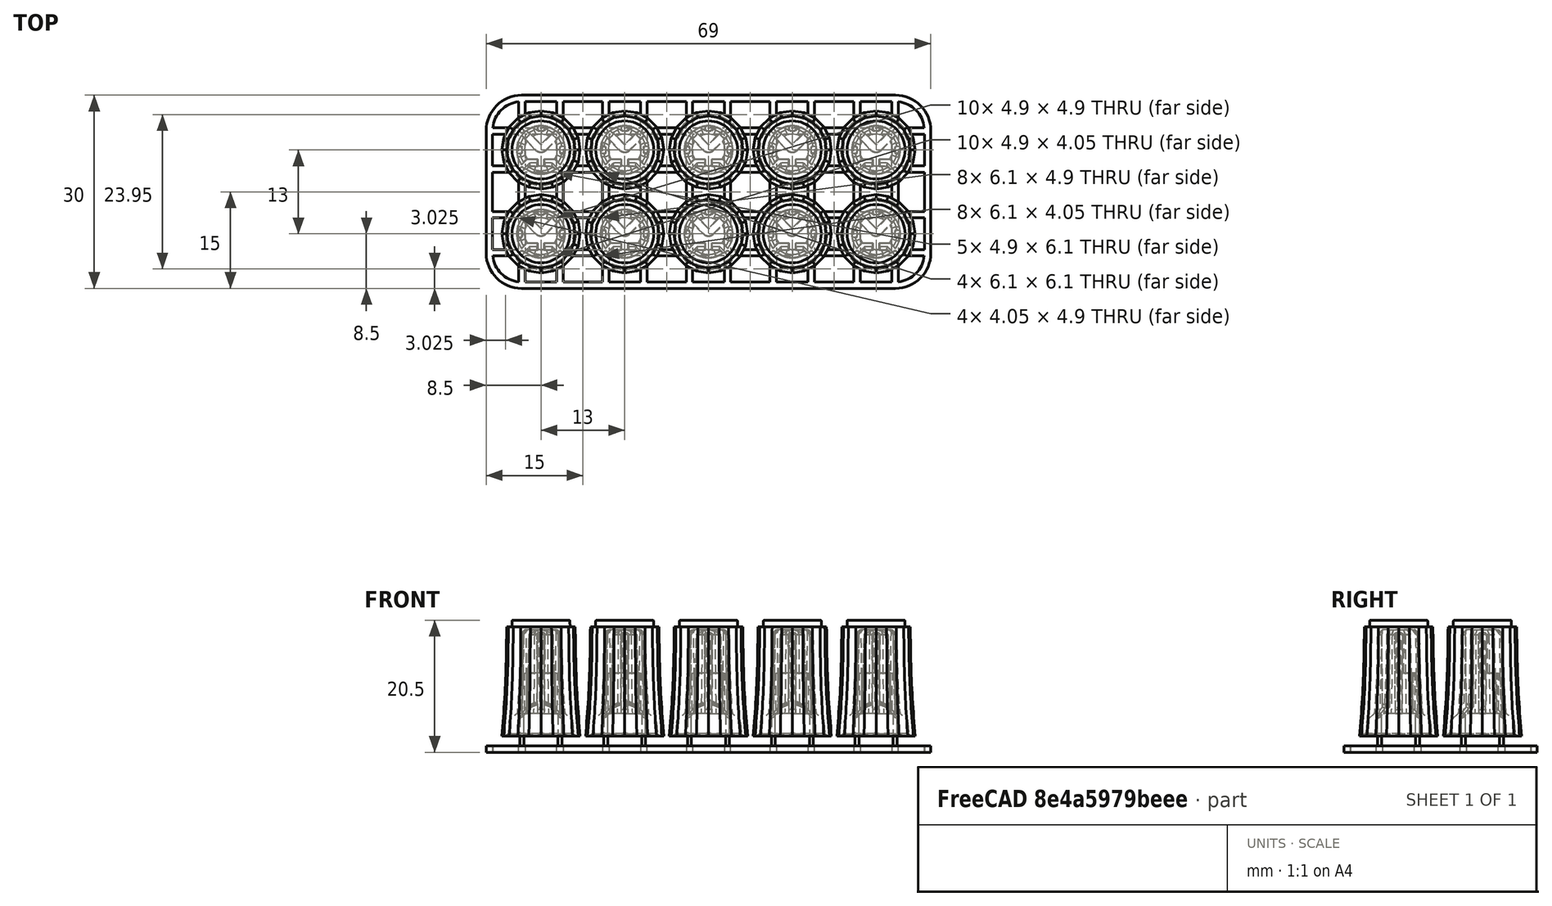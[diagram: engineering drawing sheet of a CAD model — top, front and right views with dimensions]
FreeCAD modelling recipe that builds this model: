
FCSTD DOCUMENT  (FreeCAD 1.0R38641 +678 (Git))
Label: PLASTIC-KNOB-ENC_printable
License: All rights reserved
LicenseURL: https://en.wikipedia.org/wiki/All_rights_reserved
objects: TechDraw::DrawViewDimension×11, TechDraw::DrawHatch×10, Sketcher::SketchObject×8, TechDraw::DrawViewBalloon×5, PartDesign::Pad×5, TechDraw::DrawViewPart×5, PartDesign::PolarPattern×3, TechDraw::DrawViewAnnotation×2, PartDesign::Pocket×2, PartDesign::Plane×2, PartDesign::LinearPattern×2, Part::Feature×1, PartDesign::Boolean×1, TechDraw::DrawSVGTemplate×1, PartDesign::Mirrored×1, PartDesign::CoordinateSystem×1, PartDesign::MultiTransform×1, PartDesign::Body×1, TechDraw::DrawComplexSection×1, TechDraw::DrawPage×1
note: 79 computed .brp shape members not serialized (recipe doc carries the construction recipe); baked Part::Feature solids carry a one-line shape summary decoded from their .brp

FEATURE [Part::Feature] Part__Feature  label="potmeter"
  shape: bbox 15.71 x 15.32 x 34.99 mm, 134 faces (baked)
FEATURE [PartDesign::Boolean] Boolean
  Group = -> [Part__Feature]
  Suppressed = false
  Type = 0
  UsePlacement = false
FEATURE [TechDraw::DrawSVGTemplate] Template
  EditableTexts = COLOR=Black - RAL code: 9004; CreationDate=2025-07-31; E.G.APPROVED=APPROVED; FC-Scale=5:1; FC-Title=PLASTIC - KNOB - POT; IntechStudioLtd.=Intech Studio Ltd.; MATERIAL=ABS - Terluran GP22; REV=03; STANDARD=DIN 16742-TG4
  Height = 297
  Orientation = 1
  Template = <userpath>/Documents/grid-hardware/Manufacturing/FreeCAD_technical_drawing_template/A3_LandscapeTD_MODIFIED.svg
  Width = 420
FEATURE [Sketcher::SketchObject] Sketch
  ArcFitTolerance = 0
  AttachmentSupport = -> [XZ_Plane]
  FullyConstrained = true
  MakeInternals = false
  MapMode = 5
  Placement = pos=(0,0,0) rot=(1,0,0;1.5708rad)
  sketch-geometry (1):
    g0: LineSegment StartX=0 StartY=19 StartZ=0 EndX=0 EndY=-1 EndZ=0
  constraints (4):
    c: PointOnObject(g0,g-2)
    c: Vertical(g0)
    c: DistanceY(g0,g0) = 20
    c: DistanceY(g0,g-1) = 1
FEATURE [TechDraw::DrawViewDimension] Dimension010
  AngleOverride = false
  Arbitrary = false
  ArbitraryTolerances = false
  EqualTolerance = true
  ExtensionAngle = 0
  FormatSpec = %.2w
  FormatSpecOverTolerance = %+.2w
  FormatSpecUnderTolerance = %+.2w
  Inverted = false
  LineAngle = 0
  LockPosition = false
  MeasureType = 1
  OverTolerance = 0
  Rotation = 0
  ScaleType = 0
  TheoreticalExact = false
  Type = 2
  UnderTolerance = 0
  X = -41.9183
  Y = 15.656
FEATURE [TechDraw::DrawViewAnnotation] Annotation001
  Font = osifont
  LineSpace = 100
  LockPosition = false
  MaxWidth = -1
  Rotation = 0
  ScaleType = 0
  Text = AESTHETICAL SURFACES: | COLORED BLUE ON THE ISOMETRIC VIEWS: SPI - D2 | NO BURRS, NO PARTING LINES, | NO EJECTION MARKS | FREE OF ANY DEFECTS | FREE OF ANY WELD OR MELD LINES | NON VISIBLE GATE LOCATION ALLOWED | REMAINING BLACK SURFACES: SPI - B2
  TextSize = 3
  TextStyle = 0
  X = 264.167
  Y = 100.12
FEATURE [TechDraw::DrawViewDimension] Dimension012
  AngleOverride = false
  Arbitrary = false
  ArbitraryTolerances = false
  EqualTolerance = true
  ExtensionAngle = 0
  FormatSpec = (%.2w)
  FormatSpecOverTolerance = %+.2w
  FormatSpecUnderTolerance = %+.2w
  Inverted = false
  LineAngle = 0
  LockPosition = false
  MeasureType = 1
  OverTolerance = 0
  Rotation = 0
  ScaleType = 0
  TheoreticalExact = false
  Type = 2
  UnderTolerance = 0
  X = -37.4834
  Y = -5.49655
FEATURE [TechDraw::DrawViewBalloon] Balloon004
  BubbleShape = 2
  EndType = 6
  EndTypeScale = 1
  KinkLength = 0
  LockPosition = false
  OriginX = -50.6224
  OriginY = 14.8162
  Rotation = 0
  ScaleType = 0
  ShapeScale = 1
  SourceView = -> Dimension010
  Text = 2
  TextWrapLen = -1
  X = -51.7505
  Y = 12.4076
FEATURE [TechDraw::DrawViewAnnotation] Annotation002
  Font = osifont
  LineSpace = 100
  LockPosition = false
  MaxWidth = -1
  Rotation = 0
  ScaleType = 0
  Text = Section A-A
  TextSize = 4
  TextStyle = 0
  X = 193.568
  Y = 128.632
FEATURE [Sketcher::SketchObject] Sketch008
  ArcFitTolerance = 0
  AttachmentSupport = -> [XY_Plane]
  FullyConstrained = true
  MakeInternals = false
  MapMode = 5
  sketch-geometry (6):
    g0: ArcOfCircle CenterX=0 CenterY=0 CenterZ=0 NormalX=0 NormalY=0 NormalZ=1 AngleXU=0 Radius=2.95 StartAngle=0.615084 EndAngle=0.955712
    g1: LineSegment StartX=2.40934 StartY=1.70223 StartZ=0 EndX=2.05578 EndY=1.34868 EndZ=0
    g2: LineSegment StartX=2.05578 StartY=1.34868 StartZ=0 EndX=1.34868 EndY=2.05578 EndZ=0
    g3: LineSegment StartX=1.34868 StartY=2.05578 StartZ=0 EndX=1.70223 EndY=2.40934 EndZ=0
    g4: LineSegment [constr] StartX=2.08597 StartY=2.08597 StartZ=0 EndX=0 EndY=0 EndZ=0
    g5: GeomPoint [constr] X=1.70223 Y=1.70223 Z=0
  constraints (16):
    c: Coincident(g0,g-1)
    c: Diameter(g0) = 5.9
    c: Coincident(g2,g1)
    c: Coincident(g3,g2)
    c: PointOnObject(g4,g0)
    c: Coincident(g4,g0)
    c: Angle(g4,g-2) = 0.785398
    c: Parallel(g1,g4)
    c: Parallel(g4,g3)
    c: Perpendicular(g1,g2)
    c: Symmetric(g1,g2,g5)
    c: PointOnObject(g5,g4)
    c: Distance(g2) = 1
    c: Distance(g3) = 0.5
    c: Coincident(g0,g3)
    c: Coincident(g0,g1)
FEATURE [PartDesign::Pocket] Pocket
  BaseFeature = -> Boolean
  Direction = (0,0,-1)
  Length = 9.8
  Length2 = 5
  Profile = -> Sketch008
  ReferenceAxis = -> Sketch008 [N_Axis]
  Refine = true
  Reversed = true
  Suppressed = false
  Type = 0
FEATURE [PartDesign::Mirrored] Mirrored
  BaseFeature = -> Pocket
  MirrorPlane = -> Sketch008 [V_Axis]
  Originals = -> [Pocket]
  Refine = true
  Suppressed = false
  TransformMode = 0
FEATURE [Sketcher::SketchObject] Sketch009
  ArcFitTolerance = 0
  AttachmentSupport = -> [XY_Plane]
  FullyConstrained = true
  MakeInternals = false
  MapMode = 5
  sketch-geometry (5):
    g0: ArcOfCircle CenterX=0 CenterY=0 CenterZ=0 NormalX=0 NormalY=0 NormalZ=1 AngleXU=0 Radius=2.95 StartAngle=6.11287 EndAngle=6.4535
    g1: LineSegment StartX=2.90732 StartY=0.5 StartZ=0 EndX=2.40732 EndY=0.5 EndZ=0
    g2: LineSegment StartX=2.40732 StartY=0.5 StartZ=0 EndX=2.40732 EndY=-0.5 EndZ=0
    g3: LineSegment StartX=2.40732 StartY=-0.5 StartZ=0 EndX=2.90732 EndY=-0.5 EndZ=0
    g4: GeomPoint [constr] X=2.40732 Y=0 Z=0
  constraints (13):
    c: Coincident(g0,g-1)
    c: Diameter(g0) = 5.9
    c: Horizontal(g1)
    c: Coincident(g2,g1)
    c: Vertical(g2)
    c: Horizontal(g3)
    c: Coincident(g2,g3)
    c: Symmetric(g1,g2,g4)
    c: PointOnObject(g4,g-1)
    c: DistanceX(g1,g1) = 0.5
    c: DistanceY(g2,g2) = 1
    c: Coincident(g0,g1)
    c: Coincident(g0,g3)
FEATURE [PartDesign::Pocket] Pocket001
  BaseFeature = -> Mirrored
  Direction = (0,0,-1)
  Length = 16.5
  Length2 = 5
  Profile = -> Sketch009
  ReferenceAxis = -> Sketch009 [N_Axis]
  Refine = true
  Reversed = true
  Suppressed = false
  Type = 0
FEATURE [PartDesign::Plane] DatumPlane
  AttachmentOffset = pos=(0,0,0) rot=(0,-1,0;0.15708rad)
  AttachmentSupport = -> [XZ_Plane]
  Length = 105.854
  MapMode = 5
  Placement = pos=(0,0,0) rot=(0.993863,-0.078219,-0.078219;1.57695rad)
  ResizeMode = 0
  Width = 63.5845
FEATURE [Sketcher::SketchObject] Sketch010
  ArcFitTolerance = 0
  AttachmentSupport = -> [DatumPlane]
  FullyConstrained = true
  MakeInternals = false
  MapMode = 5
  Placement = pos=(0,0,0) rot=(0.993863,-0.078219,-0.078219;1.57695rad)
  sketch-geometry (3):
    g0: LineSegment StartX=2.50536 StartY=16.5 StartZ=0 EndX=3.50536 EndY=15.4768 EndZ=0
    g1: LineSegment StartX=2.50536 StartY=16.5 StartZ=0 EndX=3.50536 EndY=16.5 EndZ=0
    g2: LineSegment StartX=3.50536 StartY=16.5 StartZ=0 EndX=3.50536 EndY=15.4768 EndZ=0
  constraints (9):
    c: DistanceY(g-1,g0) = 16.5
    c: DistanceX(g-1,g0) = 2.50536
    c: DistanceX(g0,g0) = 1
    c: Coincident(g1,g0)
    c: Coincident(g2,g1)
    c: Coincident(g2,g0)
    c: Horizontal(g1)
    c: Vertical(g2)
    c: Angle(g0,g1) = 0.796848
FEATURE [PartDesign::PolarPattern] PolarPattern
  Angle = 180
  Axis = -> Sketch009 [N_Axis]
  BaseFeature = -> Pocket001
  Mode = 0
  Occurrences = 3
  Offset = 120
  Originals = -> [Pocket001]
  Refine = true
  Suppressed = false
  TransformMode = 0
FEATURE [PartDesign::Pad] Pad001
  BaseFeature = -> PolarPattern
  Direction = (-0.156434,-0.987688,0)
  Length = 2
  Length2 = 10
  Midplane = true
  Profile = -> Sketch010
  ReferenceAxis = -> Sketch010 [N_Axis]
  Suppressed = false
  Type = 0
FEATURE [PartDesign::Plane] DatumPlane001
  AttachmentOffset = pos=(0,0,0) rot=(0,1,0;0.15708rad)
  AttachmentSupport = -> [XZ_Plane]
  Length = 105.854
  MapMode = 5
  Placement = pos=(0,0,0) rot=(0.993863,0.078219,0.078219;1.57695rad)
  ResizeMode = 0
  Width = 63.5845
FEATURE [Sketcher::SketchObject] Sketch011
  ArcFitTolerance = 0
  AttachmentSupport = -> [DatumPlane001]
  FullyConstrained = true
  MakeInternals = false
  MapMode = 5
  Placement = pos=(0,0,0) rot=(0.993863,0.078219,0.078219;1.57695rad)
  sketch-geometry (3):
    g0: LineSegment StartX=2.50536 StartY=16.5 StartZ=0 EndX=3.50536 EndY=15.4768 EndZ=0
    g1: LineSegment StartX=3.50536 StartY=15.4768 StartZ=0 EndX=3.50536 EndY=16.5 EndZ=0
    g2: LineSegment StartX=3.50536 StartY=16.5 StartZ=0 EndX=2.50536 EndY=16.5 EndZ=0
  constraints (9):
    c: Coincident(g1,g0)
    c: Vertical(g1)
    c: Coincident(g2,g1)
    c: Coincident(g2,g0)
    c: Horizontal(g2)
    c: DistanceX(g0,g0) = 1
    c: DistanceY(g-1,g0) = 16.5
    c: DistanceX(g-1,g0) = 2.50536
    c: Angle(g0,g2) = 0.796848
FEATURE [PartDesign::Pad] Pad002
  BaseFeature = -> Pad001
  Direction = (0.156434,-0.987688,0)
  Length = 2
  Length2 = 10
  Midplane = true
  Profile = -> Sketch011
  ReferenceAxis = -> Sketch011 [N_Axis]
  Suppressed = false
  Type = 0
FEATURE [PartDesign::PolarPattern] PolarPattern001
  Angle = 180
  Axis = -> Z_Axis
  BaseFeature = -> Pad002
  Mode = 0
  Occurrences = 3
  Offset = 120
  Originals = -> [Pad001,Pad002]
  Suppressed = false
  TransformMode = 0
FEATURE [PartDesign::CoordinateSystem] LCS_1
  AttacherType = Attacher::AttachEngine3D
  AttachmentSupport = -> [PolarPattern001]
  MapMode = 5
  Placement = pos=(0,0,9.8) rot=(1,0,0;3.14159rad)
FEATURE [Sketcher::SketchObject] Sketch012
  ArcFitTolerance = 1e-06
  AttachmentOffset = pos=(0,0,-3.5) rot=(0,0,1;0rad)
  AttachmentSupport = -> [XY_Plane]
  FullyConstrained = true
  MakeInternals = false
  MapMode = 5
  Placement = pos=(0,0,3.5) rot=(0,1,0;3.14159rad)
  sketch-geometry (9):
    g0: LineSegment [constr] StartX=2.95 StartY=-2.95 StartZ=0 EndX=2.95 EndY=2.95 EndZ=0
    g1: LineSegment [constr] StartX=2.95 StartY=2.95 StartZ=0 EndX=-2.95 EndY=2.95 EndZ=0
    g2: LineSegment [constr] StartX=-2.95 StartY=2.95 StartZ=0 EndX=-2.95 EndY=-2.95 EndZ=0
    g3: LineSegment [constr] StartX=-2.95 StartY=-2.95 StartZ=0 EndX=2.95 EndY=-2.95 EndZ=0
    g4: GeomPoint [constr] X=0 Y=0 Z=0
    g5: Circle CenterX=-2.95 CenterY=2.95 CenterZ=0 NormalX=0 NormalY=0 NormalZ=1 AngleXU=0 Radius=0.3
    g6: Circle CenterX=2.95 CenterY=2.95 CenterZ=0 NormalX=0 NormalY=0 NormalZ=1 AngleXU=0 Radius=0.3
    g7: Circle CenterX=2.95 CenterY=-2.95 CenterZ=0 NormalX=0 NormalY=0 NormalZ=1 AngleXU=0 Radius=0.3
    g8: Circle CenterX=-2.95 CenterY=-2.95 CenterZ=0 NormalX=0 NormalY=0 NormalZ=1 AngleXU=0 Radius=0.3
  constraints (20):
    c: Coincident(g0,g1)
    c: Coincident(g1,g2)
    c: Coincident(g2,g3)
    c: Coincident(g3,g0)
    c: Vertical(g0)
    c: Vertical(g2)
    c: Horizontal(g1)
    c: Horizontal(g3)
    c: Symmetric(g2,g0,g4)
    c: Coincident(g4,g-1)
    c: DistanceX(g3,g3) = 5.9
    c: Equal(g0,g3)
    c: Coincident(g5,g1)
    c: Coincident(g6,g0)
    c: Coincident(g7,g0)
    c: Coincident(g8,g2)
    c: Equal(g5,g6)
    c: Equal(g6,g7)
    c: Equal(g7,g8)
    c: Diameter(g5) = 0.6
FEATURE [PartDesign::Pad] Pad
  BaseFeature = -> PolarPattern001
  Direction = (0,0,-1)
  Length = 5
  Length2 = 10
  Profile = -> Sketch012
  ReferenceAxis = -> Sketch012 [N_Axis]
  Refine = true
  Suppressed = false
  Type = 0
FEATURE [Sketcher::SketchObject] Sketch013
  ArcFitTolerance = 1e-06
  AttachmentSupport = -> [Pad]
  FullyConstrained = true
  MakeInternals = false
  MapMode = 5
  Placement = pos=(0,0,-1.5) rot=(1,0,0;3.14159rad)
  sketch-geometry (10):
    g0: LineSegment StartX=-8 StartY=3.45 StartZ=0 EndX=-8 EndY=2.45 EndZ=0
    g1: LineSegment StartX=-8 StartY=2.45 StartZ=0 EndX=8 EndY=2.45 EndZ=0
    g2: LineSegment StartX=8 StartY=2.45 StartZ=0 EndX=8 EndY=3.45 EndZ=0
    g3: LineSegment StartX=8 StartY=3.45 StartZ=0 EndX=-8 EndY=3.45 EndZ=0
    g4: GeomPoint [constr] X=0 Y=2.95 Z=0
    g5: LineSegment StartX=-8 StartY=-2.45 StartZ=0 EndX=-8 EndY=-3.45 EndZ=0
    g6: LineSegment StartX=-8 StartY=-3.45 StartZ=0 EndX=8 EndY=-3.45 EndZ=0
    g7: LineSegment StartX=8 StartY=-3.45 StartZ=0 EndX=8 EndY=-2.45 EndZ=0
    g8: LineSegment StartX=8 StartY=-2.45 StartZ=0 EndX=-8 EndY=-2.45 EndZ=0
    g9: GeomPoint [constr] X=0 Y=-2.95 Z=0
  constraints (26):
    c: Coincident(g0,g1)
    c: Coincident(g1,g2)
    c: Coincident(g2,g3)
    c: Coincident(g3,g0)
    c: Vertical(g0)
    c: Vertical(g2)
    c: Horizontal(g1)
    c: Horizontal(g3)
    c: Symmetric(g2,g0,g4)
    c: PointOnObject(g4,g-2)
    c: Coincident(g5,g6)
    c: Coincident(g6,g7)
    c: Coincident(g7,g8)
    c: Coincident(g8,g5)
    c: Vertical(g5)
    c: Vertical(g7)
    c: Horizontal(g6)
    c: Horizontal(g8)
    c: Symmetric(g7,g5,g9)
    c: PointOnObject(g9,g-2)
    c: Equal(g0,g5)
    c: DistanceX(g3,g3) = 16
    c: DistanceY(g0,g0) = 1
    c: Equal(g8,g1)
    c: DistanceY(g9,g-1) = 2.95
    c: DistanceY(g-1,g4) = 2.95
FEATURE [PartDesign::Pad] Pad003
  BaseFeature = -> Pad
  Direction = (0,0,-1)
  Length = 1
  Length2 = 10
  Profile = -> Sketch013
  ReferenceAxis = -> Sketch013 [N_Axis]
  Refine = true
  Suppressed = false
  Type = 0
FEATURE [PartDesign::PolarPattern] PolarPattern002
  Angle = 90
  Axis = -> Sketch013 [N_Axis]
  BaseFeature = -> Pad003
  Mode = 0
  Occurrences = 2
  Offset = 120
  Originals = -> [Pad003]
  Refine = true
  Suppressed = false
  TransformMode = 0
FEATURE [PartDesign::LinearPattern] LinearPattern
  Direction = -> X_Axis
  Length = 52
  Mode = 1
  Occurrences = 5
  Offset = 13
  Refine = true
  Suppressed = false
  TransformMode = 0
FEATURE [PartDesign::LinearPattern] LinearPattern001
  Direction = -> Y_Axis
  Length = 13
  Mode = 0
  Occurrences = 2
  Offset = 13
  Refine = true
  Suppressed = false
  TransformMode = 0
FEATURE [PartDesign::MultiTransform] MultiTransform
  BaseFeature = -> PolarPattern002
  Refine = true
  Suppressed = false
  TransformMode = 1
  Transformations = -> [LinearPattern,LinearPattern001]
FEATURE [Sketcher::SketchObject] Sketch014
  ArcFitTolerance = 1e-06
  AttachmentSupport = -> [MultiTransform]
  FullyConstrained = true
  MakeInternals = false
  MapMode = 5
  Placement = pos=(0,0,-2.5) rot=(1,0,0;3.14159rad)
  sketch-geometry (18):
    g0: LineSegment StartX=-3 StartY=-20.5 StartZ=0 EndX=55 EndY=-20.5 EndZ=0
    g1: LineSegment StartX=59.5 StartY=-16 StartZ=0 EndX=59.5 EndY=3 EndZ=0
    g2: LineSegment StartX=55 StartY=7.5 StartZ=0 EndX=-3 EndY=7.5 EndZ=0
    g3: LineSegment StartX=-7.5 StartY=3 StartZ=0 EndX=-7.5 EndY=-16 EndZ=0
    g4: ArcOfCircle CenterX=-3 CenterY=-16 CenterZ=0 NormalX=0 NormalY=0 NormalZ=1 AngleXU=0 Radius=4.5 StartAngle=3.14159 EndAngle=4.71239
    g5: ArcOfCircle CenterX=55 CenterY=-16 CenterZ=0 NormalX=0 NormalY=0 NormalZ=1 AngleXU=0 Radius=4.5 StartAngle=4.71239 EndAngle=6.28319
    g6: ArcOfCircle CenterX=55 CenterY=3 CenterZ=0 NormalX=0 NormalY=0 NormalZ=1 AngleXU=0 Radius=4.5 StartAngle=0 EndAngle=1.5708
    g7: ArcOfCircle CenterX=-3 CenterY=3 CenterZ=0 NormalX=0 NormalY=0 NormalZ=1 AngleXU=0 Radius=4.5 StartAngle=1.5708 EndAngle=3.14159
    g8: LineSegment StartX=-3 StartY=-21.5 StartZ=0 EndX=55 EndY=-21.5 EndZ=0
    g9: LineSegment StartX=60.5 StartY=-16 StartZ=0 EndX=60.5 EndY=3 EndZ=0
    g10: LineSegment StartX=55 StartY=8.5 StartZ=0 EndX=-3 EndY=8.5 EndZ=0
    g11: LineSegment StartX=-8.5 StartY=3 StartZ=0 EndX=-8.5 EndY=-16 EndZ=0
    g12: ArcOfCircle CenterX=-3 CenterY=-16 CenterZ=0 NormalX=0 NormalY=0 NormalZ=1 AngleXU=0 Radius=5.5 StartAngle=3.14159 EndAngle=4.71239
    g13: ArcOfCircle CenterX=55 CenterY=-16 CenterZ=0 NormalX=0 NormalY=0 NormalZ=1 AngleXU=0 Radius=5.5 StartAngle=4.71239 EndAngle=6.28319
    g14: ArcOfCircle CenterX=55 CenterY=3 CenterZ=0 NormalX=0 NormalY=0 NormalZ=1 AngleXU=0 Radius=5.5 StartAngle=0 EndAngle=1.5708
    g15: ArcOfCircle CenterX=-3 CenterY=3 CenterZ=0 NormalX=0 NormalY=0 NormalZ=1 AngleXU=0 Radius=5.5 StartAngle=1.5708 EndAngle=3.14159
    g16: GeomPoint [constr] X=59.5 Y=7.5 Z=0
    g17: GeomPoint [constr] X=26 Y=-6.5 Z=0
  constraints (39):
    c: Tangent(g0,g4) = -1.5708
    c: Tangent(g0,g5) = -1.5708
    c: Tangent(g1,g5) = -1.5708
    c: Tangent(g1,g6) = -1.5708
    c: Tangent(g2,g6) = -1.5708
    c: Tangent(g2,g7) = -1.5708
    c: Tangent(g3,g7) = -1.5708
    c: Tangent(g3,g4) = -1.5708
    c: Horizontal(g0)
    c: Horizontal(g2)
    c: Vertical(g1)
    c: Vertical(g3)
    c: Equal(g4,g5)
    c: Equal(g5,g6)
    c: Equal(g6,g7)
    c: Tangent(g8,g12) = -1.5708
    c: Tangent(g8,g13) = -1.5708
    c: Tangent(g9,g13) = -1.5708
    c: Tangent(g9,g14) = -1.5708
    c: Tangent(g10,g14) = -1.5708
    c: Tangent(g10,g15) = -1.5708
    c: Tangent(g11,g15) = -1.5708
    c: Tangent(g11,g12) = -1.5708
    c: Coincident(g4,g12)
    c: Coincident(g5,g13)
    c: Coincident(g6,g14)
    c: Coincident(g7,g15)
    c: Horizontal(g8)
    c: Horizontal(g10)
    c: Vertical(g9)
    c: Symmetric(g2,g0,g17)
    c: PointOnObject(g16,g1)
    c: PointOnObject(g16,g2)
    c: DistanceY(g-1,g7) = 3
    c: DistanceX(g7,g-1) = 3
    c: DistanceY(g7,g2) = 4.5
    c: DistanceY(g2,g10) = 1
    c: DistanceY(g4,g-1) = 16
    c: DistanceX(g-1,g6) = 55
FEATURE [PartDesign::Pad] Pad004
  BaseFeature = -> MultiTransform
  Direction = (0,0,-1)
  Length = 1
  Length2 = 10
  Profile = -> Sketch014
  ReferenceAxis = -> Sketch014 [N_Axis]
  Refine = true
  Reversed = true
  Suppressed = false
  Type = 0
FEATURE [PartDesign::Body] Body  label="PLASTIC-KNOB-ENC_v2"
  AllowCompound = false
  Group = -> [Boolean,Sketch,Sketch008,Pocket,Mirrored,Sketch009,Pocket001,DatumPlane,Sketch010,PolarPattern,Pad001,DatumPlane001,Sketch011,Pad002,PolarPattern001,LCS_1,Sketch012,Pad,Sketch013,Pad003,PolarPattern002,MultiTransform,LinearPattern,LinearPattern001,Sketch014,Pad004]
  Origin = -> Origin
  Tip = -> Pad004
FEATURE [TechDraw::DrawViewPart] View
  CoarseView = false
  Direction = (0,-1,0)
  Focus = 100
  HardHidden = false
  IsoCount = 0
  IsoHidden = false
  IsoVisible = true
  LockPosition = false
  Perspective = false
  Rotation = 0
  Scale = 5
  ScaleType = 2
  ScrubCount = 0
  SeamHidden = false
  SeamVisible = true
  SmoothHidden = false
  SmoothVisible = true
  Source = -> [Body]
  X = 98.421
  XDirection = (1,0,-1e-06)
  Y = 192.804
FEATURE [TechDraw::DrawComplexSection] ComplexSection  label="Section A - A"
  BaseView = -> View
  CoarseView = false
  CutSurfaceDisplay = 2
  CuttingToolWireObject = -> Sketch
  Direction = (-1,0,1e-06)
  FileGeomPattern = C:/Program Files/FreeCAD 0.21/data/Mod/TechDraw/PAT/FCPAT.pat
  FileHatchPattern = C:/Program Files/FreeCAD 0.21/data/Mod/TechDraw/Patterns/simple.svg
  Focus = 100
  FuseBeforeCut = false
  HardHidden = false
  HatchOffset = (0,0,0)
  HatchRotation = 0
  HatchScale = 1
  IsoCount = 0
  IsoHidden = false
  IsoVisible = false
  LockPosition = false
  NameGeomPattern = Gyémánt bevonatú
  Perspective = false
  ProjectionStrategy = 0
  Rotation = -90
  Scale = 5
  ScaleType = 2
  ScrubCount = 0
  SeamHidden = false
  SeamVisible = true
  SectionDirection = 4
  SectionLineStretch = 1
  SectionNormal = (-1,0,1e-06)
  SectionOrigin = (0,0,0)
  SectionSymbol = A
  SmoothHidden = false
  SmoothVisible = true
  Source = -> [Body]
  TrimAfterCut = false
  UsePreviousCut = false
  X = 193.568
  XDirection = (-1e-06,0,-1)
  Y = 192.821
FEATURE [TechDraw::DrawViewPart] View003
  CoarseView = false
  Direction = (-0.57735,-0.57735,0.57735)
  Focus = 100
  HardHidden = false
  IsoCount = 0
  IsoHidden = false
  IsoVisible = true
  LockPosition = false
  Perspective = false
  Rotation = 0
  Scale = 2
  ScaleType = 2
  ScrubCount = 0
  SeamHidden = false
  SeamVisible = true
  SmoothHidden = false
  SmoothVisible = true
  Source = -> [Body]
  X = 379.046
  XDirection = (0.707107,-0.707107,0)
  Y = 107.401
FEATURE [TechDraw::DrawViewPart] View004
  CoarseView = false
  Direction = (-0.57735,-0.57735,-0.57735)
  Focus = 100
  HardHidden = false
  IsoCount = 0
  IsoHidden = false
  IsoVisible = true
  LockPosition = false
  Perspective = false
  Rotation = 0
  Scale = 2
  ScaleType = 2
  ScrubCount = 0
  SeamHidden = false
  SeamVisible = true
  SmoothHidden = false
  SmoothVisible = true
  Source = -> [Body]
  X = 337.082
  XDirection = (0.707106,-0.707106,0)
  Y = 107.401
FEATURE [TechDraw::DrawHatch] Hatch001  label="Hatch001F2"
  HatchPattern = C:/Program Files/FreeCAD 0.21/data/Mod/TechDraw/Patterns/solid.svg
  Source = -> View003 [Face2,Face13,Face4,Face5,Face3,Face6,Face9,Face8,Face7,Face12,Face11,Face10]
FEATURE [TechDraw::DrawHatch] Hatch002  label="Hatch002F1"
  HatchPattern = C:/Program Files/FreeCAD 0.21/data/Mod/TechDraw/Patterns/solid.svg
  Source = -> View003 [Face1]
FEATURE [TechDraw::DrawViewBalloon] Balloon
  BubbleShape = 1
  EndType = 3
  EndTypeScale = 1
  KinkLength = 0
  LockPosition = false
  OriginX = -2.29422
  OriginY = 3.04373
  Rotation = 0
  ScaleType = 0
  ShapeScale = 1
  SourceView = -> View004
  TextWrapLen = -1
  X = -16.2526
  Y = -5.35905
FEATURE [TechDraw::DrawViewPart] View002
  CoarseView = false
  Direction = (1e-06,0,1)
  Focus = 100
  HardHidden = false
  IsoCount = 0
  IsoHidden = false
  IsoVisible = true
  LockPosition = false
  Perspective = false
  Rotation = 0
  Scale = 5
  ScaleType = 2
  ScrubCount = 0
  SeamHidden = false
  SeamVisible = true
  SmoothHidden = false
  SmoothVisible = true
  Source = -> [Body]
  X = 100.462
  XDirection = (1,0,-1e-06)
  Y = 74.8021
FEATURE [TechDraw::DrawViewDimension] Dimension009
  AngleOverride = false
  Arbitrary = false
  ArbitraryTolerances = false
  EqualTolerance = true
  ExtensionAngle = 0
  FormatSpec = 10× %.2w
  FormatSpecOverTolerance = %+.2w
  FormatSpecUnderTolerance = %+.2w
  Inverted = false
  LineAngle = 0
  LockPosition = false
  MeasureType = 1
  OverTolerance = 0
  References2D = -> [View002]
  Rotation = 0
  ScaleType = 0
  TheoreticalExact = false
  Type = 0
  UnderTolerance = 0
  X = -39.2324
  Y = 9.93901
FEATURE [TechDraw::DrawViewDimension] Dimension013
  AngleOverride = false
  Arbitrary = false
  ArbitraryTolerances = false
  EqualTolerance = true
  ExtensionAngle = 0
  FormatSpec = ⌀%.2w
  FormatSpecOverTolerance = %+.2w
  FormatSpecUnderTolerance = %+.2w
  Inverted = false
  LineAngle = 0
  LockPosition = false
  MeasureType = 1
  OverTolerance = 0
  References2D = -> [View]
  Rotation = 0
  ScaleType = 0
  TheoreticalExact = false
  Type = 1
  UnderTolerance = 0
  X = -8.9e-05
  Y = 66.4443
FEATURE [TechDraw::DrawViewDimension] Dimension014
  AngleOverride = false
  Arbitrary = false
  ArbitraryTolerances = false
  EqualTolerance = true
  ExtensionAngle = 0
  FormatSpec = %.2w
  FormatSpecOverTolerance = %+.2w
  FormatSpecUnderTolerance = %+.2w
  Inverted = false
  LineAngle = 0
  LockPosition = false
  MeasureType = 1
  OverTolerance = 0
  References2D = -> [View]
  Rotation = 0
  ScaleType = 0
  TheoreticalExact = false
  Type = 2
  UnderTolerance = 0
  X = 38.805
  Y = 45.2486
FEATURE [TechDraw::DrawViewDimension] Dimension015
  AngleOverride = false
  Arbitrary = false
  ArbitraryTolerances = false
  EqualTolerance = true
  ExtensionAngle = 0
  FormatSpec = %.2w
  FormatSpecOverTolerance = %+.2w
  FormatSpecUnderTolerance = %+.2w
  Inverted = false
  LineAngle = 0
  LockPosition = false
  MeasureType = 1
  OverTolerance = 0
  References2D = -> [View]
  Rotation = 0
  ScaleType = 0
  TheoreticalExact = false
  Type = 2
  UnderTolerance = 0
  X = -48.6863
  Y = 2.49998
FEATURE [TechDraw::DrawViewPart] View001
  CoarseView = false
  Direction = (-1e-06,0,-1)
  Focus = 100
  HardHidden = false
  IsoCount = 0
  IsoHidden = false
  IsoVisible = true
  LockPosition = false
  Perspective = false
  Rotation = 0
  Scale = 5
  ScaleType = 2
  ScrubCount = 0
  SeamHidden = false
  SeamVisible = true
  SmoothHidden = false
  SmoothVisible = true
  Source = -> [Body]
  X = 305.681
  XDirection = (1,0,-1e-06)
  Y = 190.563
FEATURE [TechDraw::DrawViewDimension] Dimension017
  AngleOverride = false
  Arbitrary = false
  ArbitraryTolerances = false
  BoxCorners = (2) [(-172.5,-75,-1e-07),(172.5,75,1e-07)]
  EqualTolerance = true
  ExtensionAngle = 0
  FormatSpec = ⌀%.2w
  FormatSpecOverTolerance = %+.2w
  FormatSpecUnderTolerance = %+.2w
  Inverted = false
  LineAngle = 0
  LockPosition = false
  MeasureType = 1
  OverTolerance = 0
  References2D = -> [View001]
  Rotation = 0
  ScaleType = 0
  TheoreticalExact = false
  Type = 5
  UnderTolerance = 0
  X = -43.4
  Y = 27.6231
FEATURE [TechDraw::DrawViewDimension] Dimension
  AngleOverride = false
  Arbitrary = false
  ArbitraryTolerances = false
  BoxCorners = (2) [(-30.374,-45,-1e-07),(30.374,45,1e-07)]
  EqualTolerance = true
  ExtensionAngle = 0
  FormatSpec = %.2w
  FormatSpecOverTolerance = %+.2w
  FormatSpecUnderTolerance = %+.2w
  Inverted = false
  LineAngle = 0
  LockPosition = false
  MeasureType = 1
  OverTolerance = 0.1
  References2D = -> [ComplexSection]
  Rotation = 0
  ScaleType = 0
  TheoreticalExact = false
  Type = 2
  UnderTolerance = -0.1
  X = 31.0773
  Y = -20.5
FEATURE [TechDraw::DrawViewDimension] Dimension021
  AngleOverride = false
  Arbitrary = false
  ArbitraryTolerances = false
  BoxCorners = (2) [(-30.374,-45,-1e-07),(30.374,45,1e-07)]
  EqualTolerance = false
  ExtensionAngle = 0
  FormatSpec = ⌀%.2w
  FormatSpecOverTolerance = %+.2w
  FormatSpecUnderTolerance = %+.2w
  Inverted = false
  LineAngle = 0
  LockPosition = false
  MeasureType = 1
  OverTolerance = 0.1
  References2D = -> [ComplexSection]
  Rotation = 0
  ScaleType = 0
  TheoreticalExact = false
  Type = 1
  UnderTolerance = 0
  X = -0.045274
  Y = -42.8297
FEATURE [TechDraw::DrawViewDimension] Dimension022
  AngleOverride = false
  Arbitrary = false
  ArbitraryTolerances = false
  BoxCorners = (2) [(-40,-30.374,-1e-07),(40,30.374,1e-07)]
  EqualTolerance = true
  ExtensionAngle = 0
  FormatSpec = %.2w
  FormatSpecOverTolerance = %+.2w
  FormatSpecUnderTolerance = %+.2w
  Inverted = false
  LineAngle = 0
  LockPosition = false
  MeasureType = 1
  OverTolerance = 0.05
  References2D = -> [View001]
  Rotation = 0
  ScaleType = 0
  TheoreticalExact = false
  Type = 1
  UnderTolerance = -0.05
  X = -5.1e-05
  Y = 54.1432
FEATURE [TechDraw::DrawViewDimension] Dimension023
  AngleOverride = false
  Arbitrary = false
  ArbitraryTolerances = false
  BoxCorners = (2) [(-30.374,-30.374,-1e-07),(30.374,30.374,1e-07)]
  EqualTolerance = true
  ExtensionAngle = 0
  FormatSpec = %.2w
  FormatSpecOverTolerance = %+.2w
  FormatSpecUnderTolerance = %+.2w
  Inverted = false
  LineAngle = 0
  LockPosition = false
  MeasureType = 1
  OverTolerance = 0.05
  References2D = -> [View001]
  Rotation = 0
  ScaleType = 0
  TheoreticalExact = false
  Type = 2
  UnderTolerance = -0.05
  X = 37.6716
  Y = 24.7624
FEATURE [TechDraw::DrawViewBalloon] Balloon009
  BubbleShape = 2
  EndType = 0
  EndTypeScale = 1
  KinkLength = 5
  LockPosition = false
  OriginX = -5.92613
  OriginY = 0.938607
  Rotation = 0
  ScaleType = 0
  ShapeScale = 1
  SourceView = -> View001
  Text = 3
  TextWrapLen = -1
  X = -11.2478
  Y = 3.14051
FEATURE [TechDraw::DrawViewBalloon] Balloon010
  BubbleShape = 2
  EndType = 0
  EndTypeScale = 1
  KinkLength = 5
  LockPosition = false
  OriginX = -1.98815
  OriginY = 12.4234
  Rotation = 0
  ScaleType = 0
  ShapeScale = 1
  SourceView = -> View001
  Text = 3
  TextWrapLen = -1
  X = -5.51177
  Y = 10.7925
FEATURE [TechDraw::DrawViewBalloon] Balloon011
  BubbleShape = 2
  EndType = 0
  EndTypeScale = 1
  KinkLength = 5
  LockPosition = false
  OriginX = 11.1664
  OriginY = -5.13173
  Rotation = 0
  ScaleType = 0
  ShapeScale = 1
  SourceView = -> View001
  Text = 3
  TextWrapLen = -1
  X = 11.5702
  Y = 3.12692
FEATURE [TechDraw::DrawPage] Page  label="PLASTIC-KNOB-ENC_Drawing"
  KeepUpdated = true
  NextBalloonIndex = 11
  ProjectionType = 0
  Template = -> Template
  Views = -> [View,View001,View002,ComplexSection,Dimension009,View003,View004,Annotation001,Balloon,Annotation002,Dimension013,Dimension014,Dimension015,Dimension017,Dimension,Dimension021,Dimension022,Dimension023,Balloon009,Balloon010,Balloon011]
FEATURE [TechDraw::DrawHatch] Hatch012
  HatchPattern = /app/share/Mod/TechDraw/Patterns/solid.svg
  Source = -> View004 [Face12,Face7,Face4,Face3,Face5,Face6,Face9]
FEATURE [TechDraw::DrawHatch] Hatch013
  HatchPattern = /app/share/Mod/TechDraw/Patterns/solid.svg
  Source = -> View004 [Face1,Face2,Face15,Face18,Face16,Face19]
FEATURE [TechDraw::DrawHatch] Hatch014
  HatchPattern = /app/share/Mod/TechDraw/Patterns/solid.svg
  Source = -> View004 [Face20,Face21,Face29,Face26,Face24,Face22,Face23,Face27,Face28]
FEATURE [TechDraw::DrawHatch] Hatch015
  HatchPattern = /app/share/Mod/TechDraw/Patterns/solid.svg
  Source = -> View004 [Face11,Face8,Face17]
FEATURE [TechDraw::DrawHatch] Hatch016
  HatchPattern = /app/share/Mod/TechDraw/Patterns/solid.svg
  Source = -> View004 [Face14]
FEATURE [TechDraw::DrawHatch] Hatch017
  HatchPattern = /app/share/Mod/TechDraw/Patterns/solid.svg
  Source = -> View004 [Face10]
FEATURE [TechDraw::DrawHatch] Hatch018
  HatchPattern = /app/share/Mod/TechDraw/Patterns/solid.svg
  Source = -> View004 [Face13]
FEATURE [TechDraw::DrawHatch] Hatch019
  HatchPattern = /app/share/Mod/TechDraw/Patterns/solid.svg
  Source = -> View004 [Face25,Face30]
